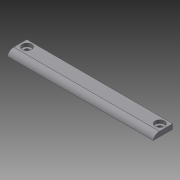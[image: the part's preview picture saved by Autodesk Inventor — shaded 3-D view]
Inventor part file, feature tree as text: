
AUTODESK INVENTOR PART (.ipt)
format: ipt  version: 2015 (Build 190159000, 159)  size: 109,568 bytes
history: native  units: mm
features: extrude x4, sketch x4, other x1, fillet x1
ambient origin geometry x8: Origin, YZ Plane, XZ Plane, XY Plane, X Axis, Y Axis, Z Axis, Center Point
bodies: Body1 (feature_tree), Body2 (feature_tree)
feature tree (10):
  other  "ソリッド1"
  extrude  "押し出し1"  Depth=90.0mm
  extrude  "押し出し2"  Depth=7.0mm
  extrude  "押し出し3"  Depth=3.0mm TaperAngle=0.0deg
  extrude  "押し出し4"  Depth=5.8mm
  fillet  "フィレット1"  Radius=5.8mm
  sketch  "スケッチ1"
  sketch  "スケッチ2"
  sketch  "スケッチ3"
  sketch  "スケッチ4"
